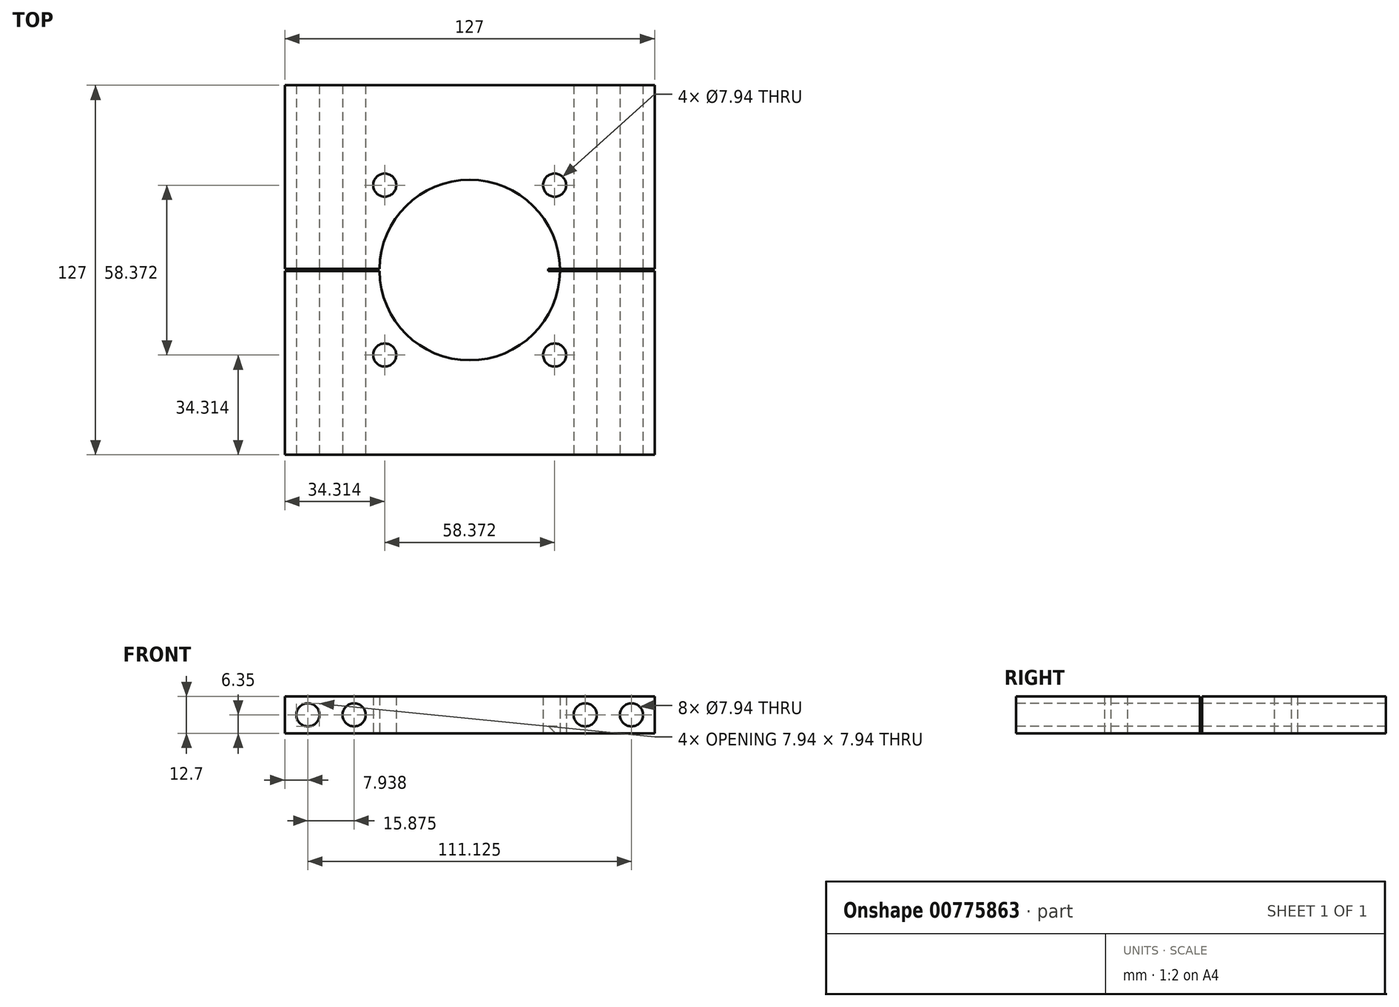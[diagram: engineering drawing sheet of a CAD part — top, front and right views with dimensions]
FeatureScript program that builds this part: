
annotation { "Feature Type Name" : "Feature", "Feature Type Description" : "" }
export const myFeature = defineFeature(function(context is Context, id is Id, definition is map)
    precondition{}
    {
        {
            var Q0;
            Q0=qCreatedBy(makeId("Top.planeOp"),FACE);
            var sketch = newSketch(context, id + "F0", { "sketchPlane" : qUnion([Q0])});
            skCircle(sketch, "E0", {"center": v(0, 0) * mm, "radius": 31 * mm});
            skLineSegment(sketch, "E1.bottom", {"start": v(-63.5, 63.5) * mm, "end": v(63.5, 63.5) * mm});
            skLineSegment(sketch, "E1.top", {"start": v(-63.5, -63.5) * mm, "end": v(63.5, -63.5) * mm});
            skLineSegment(sketch, "E1.left", {"start": v(-63.5, 63.5) * mm, "end": v(-63.5, -63.5) * mm});
            skLineSegment(sketch, "E1.right", {"start": v(63.5, 63.5) * mm, "end": v(63.5, -63.5) * mm});
            skCircle(sketch, "E2", {"center": v(0, 0) * mm, "radius": 50.8 * mm, "construction": true});
            skCircle(sketch, "E3", {"center": v(0, 0) * mm, "radius": 27 * mm});
            skLineSegment(sketch, "E4.bottom", {"start": v(-63.5, 0.4) * mm, "end": v(63.5, 0.4) * mm});
            skLineSegment(sketch, "E4.top", {"start": v(-63.5, -0.4) * mm, "end": v(63.5, -0.4) * mm});
            skLineSegment(sketch, "E4.left", {"start": v(-63.5, 0.4) * mm, "end": v(-63.5, -0.4) * mm});
            skLineSegment(sketch, "E4.right", {"start": v(63.5, 0.4) * mm, "end": v(63.5, -0.4) * mm});
            skCircle(sketch, "E5", {"center": v(-29.19, 29.19) * mm, "radius": 3.97 * mm});
            skLineSegment(sketch, "E6", {"start": v(0, 0) * mm, "end": v(-63.5, 63.5) * mm, "construction": true});
            skCircle(sketch, "E7.1.0", {"center": v(-29.19, -29.19) * mm, "radius": 3.97 * mm});
            skCircle(sketch, "E7.2.0", {"center": v(29.19, -29.19) * mm, "radius": 3.97 * mm});
            skCircle(sketch, "E7.3.0", {"center": v(29.19, 29.19) * mm, "radius": 3.97 * mm});
            skSolve(sketch);
        }
        {
            var Q0;
            {var subQ1=sQuery(id+"F0.wireOp",EDGE,"E1.bottom");Q0=makeQuery(id+"F0.imprint","IMPRINT",FACE,{"disambiguationData":[TD([[makeQuery(id+"F0.imprint","IMPRINT",EDGE,{"derivedFrom":subQ1}),-1.0]])]});}
            var Q1;
            {var subQ1=sQuery(id+"F0.wireOp",EDGE,"E1.top");Q1=makeQuery(id+"F0.imprint","IMPRINT",FACE,{"disambiguationData":[TD([[makeQuery(id+"F0.imprint","IMPRINT",EDGE,{"derivedFrom":subQ1}),1.0]])]});}
            var Q2;
            {var subQ0=sQuery(id+"F0.wireOp",EDGE,"E4.bottom");var subQ1=sQuery(id+"F0.wireOp",EDGE,"E0");var subQ2=makeQuery(id+"F0.imprint","INTERSECT",VERTEX,{"disambiguationData":[OD(0.0)],"derivedFrom":[subQ1,subQ0]});Q2=makeQuery(id+"F0.imprint","IMPRINT",FACE,{"disambiguationData":[TD([[makeQuery(id+"F0.imprint","IMPRINT",EDGE,{"disambiguationData":[TD([[subQ2,1.0]])],"derivedFrom":subQ1}),1.0]])]});}
            var Q3;
            {var subQ0=sQuery(id+"F0.wireOp",EDGE,"E4.top");var subQ1=sQuery(id+"F0.wireOp",EDGE,"E0");var subQ2=makeQuery(id+"F0.imprint","INTERSECT",VERTEX,{"disambiguationData":[OD(0.0)],"derivedFrom":[subQ1,subQ0]});Q3=makeQuery(id+"F0.imprint","IMPRINT",FACE,{"disambiguationData":[TD([[makeQuery(id+"F0.imprint","IMPRINT",EDGE,{"disambiguationData":[TD([[subQ2,-1.0]])],"derivedFrom":subQ1}),1.0]])]});}
            extrude(context, id + "F1", {"entities" : qUnion([Q0, Q1, Q2, Q3]), "endBound" : BoundingType.SYMMETRIC, "depth" : 12.7 * mm, "offsetDistance" : 25.4 * mm});
        }
        {
            var Q0;
            {var subQ0=sQuery(id+"F0.wireOp",EDGE,"E4.top");var subQ1=sQuery(id+"F0.wireOp",EDGE,"E0");var subQ2=makeQuery(id+"F0.imprint","INTERSECT",VERTEX,{"disambiguationData":[OD(0.0)],"derivedFrom":[subQ1,subQ0]});Q0=makeQuery(id+"F0.imprint","IMPRINT",FACE,{"disambiguationData":[TD([[makeQuery(id+"F0.imprint","IMPRINT",EDGE,{"disambiguationData":[TD([[subQ2,-1.0]])],"derivedFrom":subQ1}),1.0]])]});}
            var Q1;
            {var subQ0=sQuery(id+"F0.wireOp",EDGE,"E4.bottom");var subQ1=sQuery(id+"F0.wireOp",EDGE,"E0");var subQ2=makeQuery(id+"F0.imprint","INTERSECT",VERTEX,{"disambiguationData":[OD(0.0)],"derivedFrom":[subQ1,subQ0]});Q1=makeQuery(id+"F0.imprint","IMPRINT",FACE,{"disambiguationData":[TD([[makeQuery(id+"F0.imprint","IMPRINT",EDGE,{"disambiguationData":[TD([[subQ2,1.0]])],"derivedFrom":subQ1}),1.0]])]});}
            extrude(context, id + "F2", {"entities" : qUnion([Q0, Q1]), "operationType" : NewBodyOperationType.REMOVE, "oppositeDirection" : true, "depth" : 3.8 * mm, "offsetDistance" : 25.4 * mm, "hasSecondDirection" : true, "secondDirectionOppositeDirection" : false, "secondDirectionDepth" : 6.35 * mm});
        }
        {
            var Q0;
            {var subQ0=sQuery(id+"F0.wireOp",EDGE,"E4.top");var subQ1=sQuery(id+"F0.wireOp",EDGE,"E3");Q0=makeQuery(id+"F1.opExtrude","CAP_EDGE",EDGE,{"disambiguationData":[OSD([subQ1]),TDD([makeQuery(id+"F0.imprint","IMPRINT",EDGE,{"disambiguationData":[TD([[makeQuery(id+"F0.imprint","INTERSECT",VERTEX,{"disambiguationData":[OD(0.0)],"derivedFrom":[subQ1,subQ0]}),-1.0]])],"derivedFrom":subQ1})])],"isStart":true});}
            var Q1;
            {var subQ0=sQuery(id+"F0.wireOp",EDGE,"E4.bottom");var subQ1=sQuery(id+"F0.wireOp",EDGE,"E3");Q1=makeQuery(id+"F1.opExtrude","CAP_EDGE",EDGE,{"disambiguationData":[OSD([subQ1]),TDD([makeQuery(id+"F0.imprint","IMPRINT",EDGE,{"disambiguationData":[TD([[makeQuery(id+"F0.imprint","INTERSECT",VERTEX,{"disambiguationData":[OD(0.0)],"derivedFrom":[subQ1,subQ0]}),1.0]])],"derivedFrom":subQ1})])],"isStart":true});}
            chamfer(context, id + "F3", {"entities" : qUnion([Q0, Q1]), "width" : 2.54 * mm, "tangentPropagation" : true});
        }
        {
            var Q0;
            Q0=qCreatedBy(makeId("Front.planeOp"),FACE);
            var sketch = newSketch(context, id + "F4", { "sketchPlane" : qUnion([Q0])});
            skCircle(sketch, "E8", {"center": v(-39.69, 0) * mm, "radius": 3.97 * mm});
            skCircle(sketch, "E9", {"center": v(39.69, 0) * mm, "radius": 3.97 * mm});
            skLineSegment(sketch, "E10", {"start": v(-39.69, 0) * mm, "end": v(39.69, 0) * mm});
            skCircle(sketch, "E11", {"center": v(-55.56, 0) * mm, "radius": 3.97 * mm});
            skCircle(sketch, "E12", {"center": v(55.56, 0) * mm, "radius": 3.97 * mm});
            skSolve(sketch);
        }
        {
            var Q0;
            Q0=makeQuery(id+"F4.imprint","IMPRINT",FACE,{"disambiguationData":[TD([[makeQuery(id+"F4.imprint","IMPRINT",EDGE,{"derivedFrom":sQuery(id+"F4.wireOp",EDGE,"E9")}),1.0]])]});
            var Q1;
            Q1=makeQuery(id+"F4.imprint","IMPRINT",FACE,{"disambiguationData":[TD([[makeQuery(id+"F4.imprint","IMPRINT",EDGE,{"derivedFrom":sQuery(id+"F4.wireOp",EDGE,"E12")}),1.0]])]});
            var Q2;
            Q2=makeQuery(id+"F4.imprint","IMPRINT",FACE,{"disambiguationData":[TD([[makeQuery(id+"F4.imprint","IMPRINT",EDGE,{"derivedFrom":sQuery(id+"F4.wireOp",EDGE,"E8")}),1.0]])]});
            var Q3;
            Q3=makeQuery(id+"F4.imprint","IMPRINT",FACE,{"disambiguationData":[TD([[makeQuery(id+"F4.imprint","IMPRINT",EDGE,{"derivedFrom":sQuery(id+"F4.wireOp",EDGE,"E11")}),1.0]])]});
            extrude(context, id + "F5", {"entities" : qUnion([Q0, Q1, Q2, Q3]), "operationType" : NewBodyOperationType.REMOVE, "endBound" : BoundingType.SYMMETRIC, "oppositeDirection" : true, "depth" : 127 * mm, "offsetDistance" : 25.4 * mm});
        }
    });
